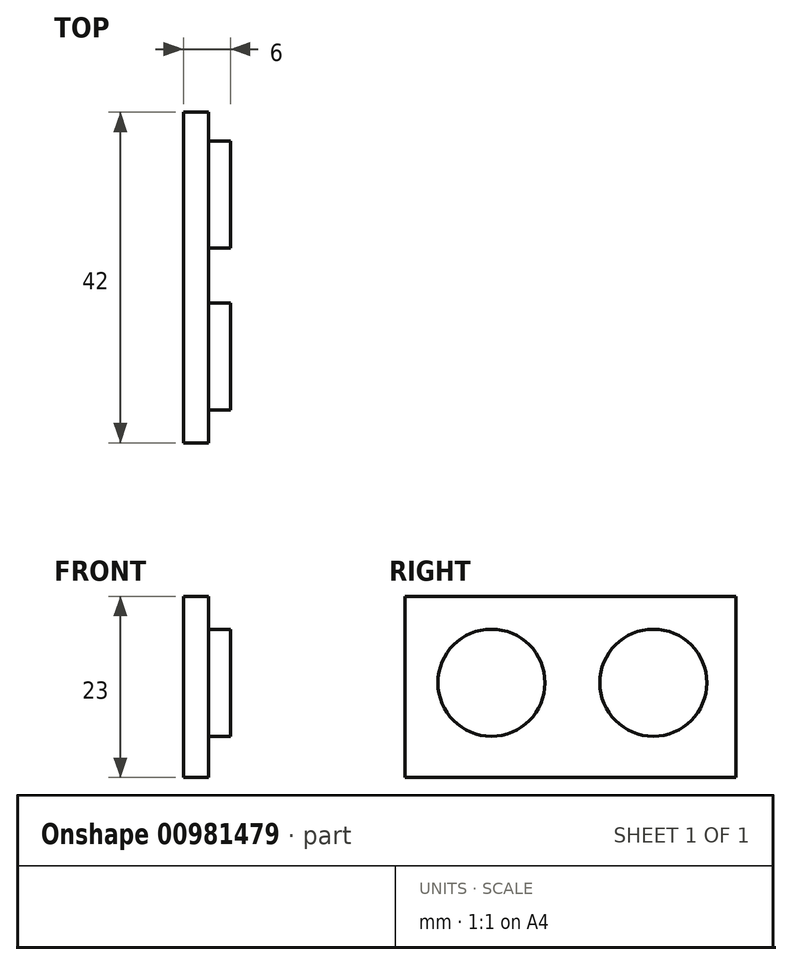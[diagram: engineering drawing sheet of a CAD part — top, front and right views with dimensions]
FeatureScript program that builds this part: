
annotation { "Feature Type Name" : "Feature", "Feature Type Description" : "" }
export const myFeature = defineFeature(function(context is Context, id is Id, definition is map)
    precondition{}
    {
        {
            var Q0;
            Q0=qCreatedBy(makeId("Right.planeOp"),FACE);
            var sketch = newSketch(context, id + "F0", { "sketchPlane" : qUnion([Q0])});
            skLineSegment(sketch, "E0.bottom", {"start": v(-25.01, 20.03) * mm, "end": v(16.99, 20.03) * mm});
            skLineSegment(sketch, "E0.top", {"start": v(-25.01, -2.97) * mm, "end": v(16.99, -2.97) * mm});
            skLineSegment(sketch, "E0.left", {"start": v(-25.01, 20.03) * mm, "end": v(-25.01, -2.97) * mm});
            skLineSegment(sketch, "E0.right", {"start": v(16.99, 20.03) * mm, "end": v(16.99, -2.97) * mm});
            skSolve(sketch);
        }
        {
            var Q0;
            Q0=makeQuery(id+"F0.imprint","IMPRINT",FACE,{"disambiguationData":[TD([[makeQuery(id+"F0.imprint","IMPRINT",EDGE,{"derivedFrom":sQuery(id+"F0.wireOp",EDGE,"E0.bottom")}),-1.0]])]});
            extrude(context, id + "F1", {"entities" : qUnion([Q0]), "depth" : 3.2 * mm, "offsetDistance" : 25 * mm});
        }
        {
            var Q0;
            Q0=qCreatedBy(makeId("Right.planeOp"),FACE);
            var sketch = newSketch(context, id + "F2", { "sketchPlane" : qUnion([Q0])});
            skCircle(sketch, "E1", {"center": v(-14.05, 9.05) * mm, "radius": 6.8 * mm});
            skCircle(sketch, "E2", {"center": v(6.52, 9.05) * mm, "radius": 6.8 * mm});
            skSolve(sketch);
        }
        {
            var Q0;
            Q0=qSketchRegion(id+"F2",true);
            extrude(context, id + "F3", {"entities" : qUnion([Q0]), "operationType" : NewBodyOperationType.ADD, "depth" : 6 * mm, "offsetDistance" : 25 * mm});
        }
    });
